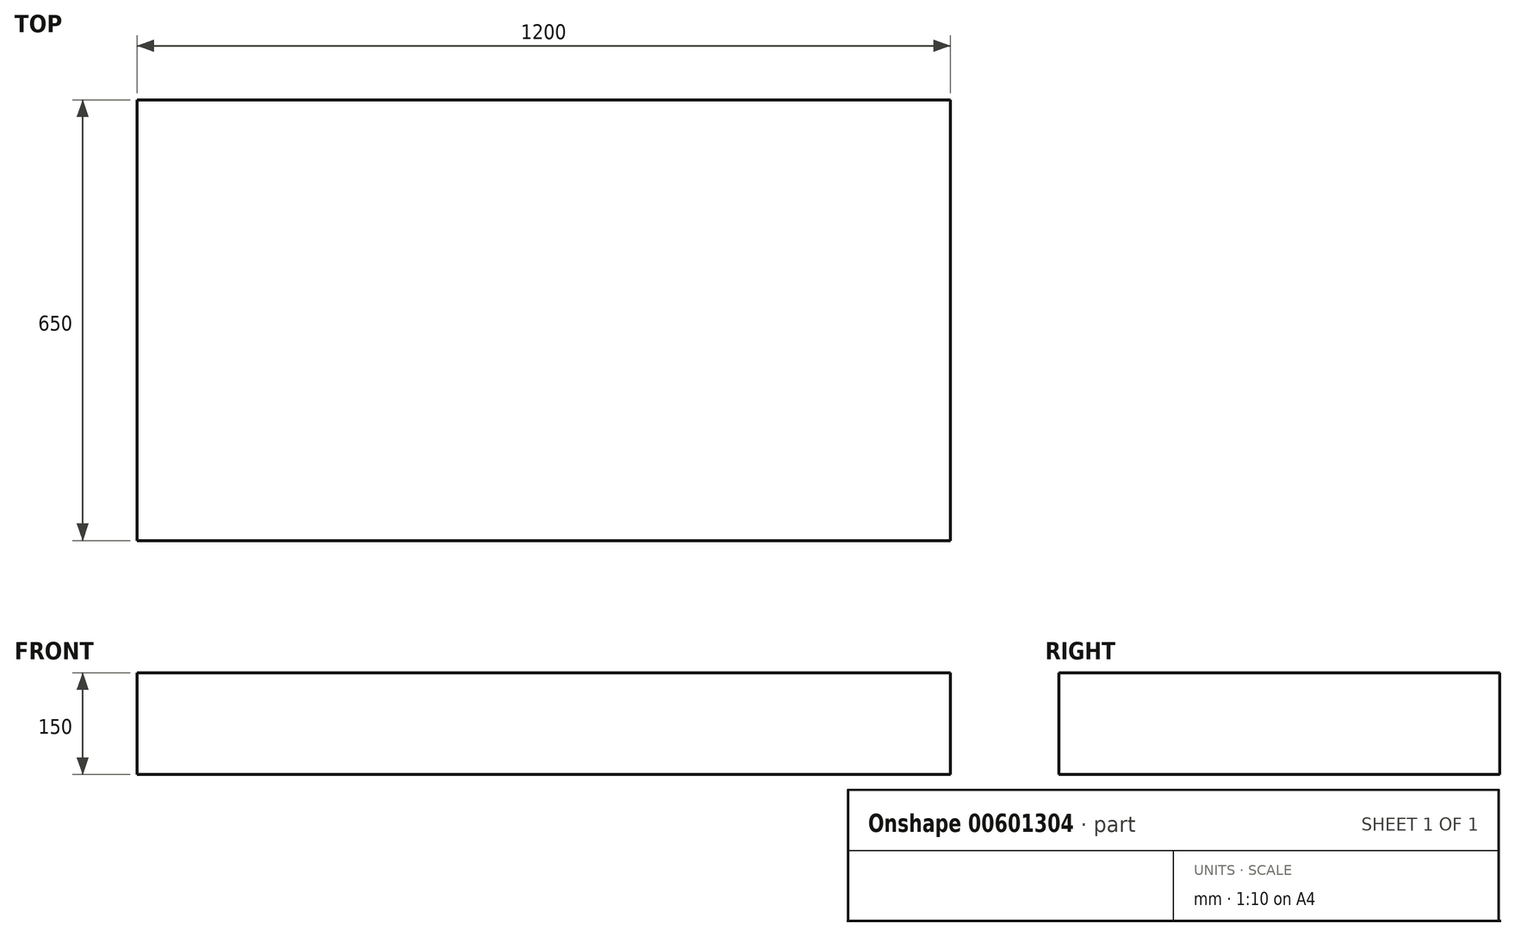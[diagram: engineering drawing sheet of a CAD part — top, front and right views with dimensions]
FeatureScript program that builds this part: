
annotation { "Feature Type Name" : "Feature", "Feature Type Description" : "" }
export const myFeature = defineFeature(function(context is Context, id is Id, definition is map)
    precondition{}
    {
        {
            var Q0;
            Q0=qCreatedBy(makeId("Top.planeOp"),FACE);
            var sketch = newSketch(context, id + "F0", { "sketchPlane" : qUnion([Q0])});
            skLineSegment(sketch, "E0.bottom", {"start": v(0, 0) * mm, "end": v(1200, 0) * mm});
            skLineSegment(sketch, "E0.top", {"start": v(0, 650) * mm, "end": v(1200, 650) * mm});
            skLineSegment(sketch, "E0.left", {"start": v(0, 0) * mm, "end": v(0, 650) * mm});
            skLineSegment(sketch, "E0.right", {"start": v(1200, 0) * mm, "end": v(1200, 650) * mm});
            skSolve(sketch);
        }
        {
            var Q0;
            Q0 = qSketchRegion(id + "F0", true);
            extrude(context, id + "F1", {"entities" : qUnion([Q0]), "depth" : 150 * mm, "offsetDistance" : 25 * mm});
        }
    });
